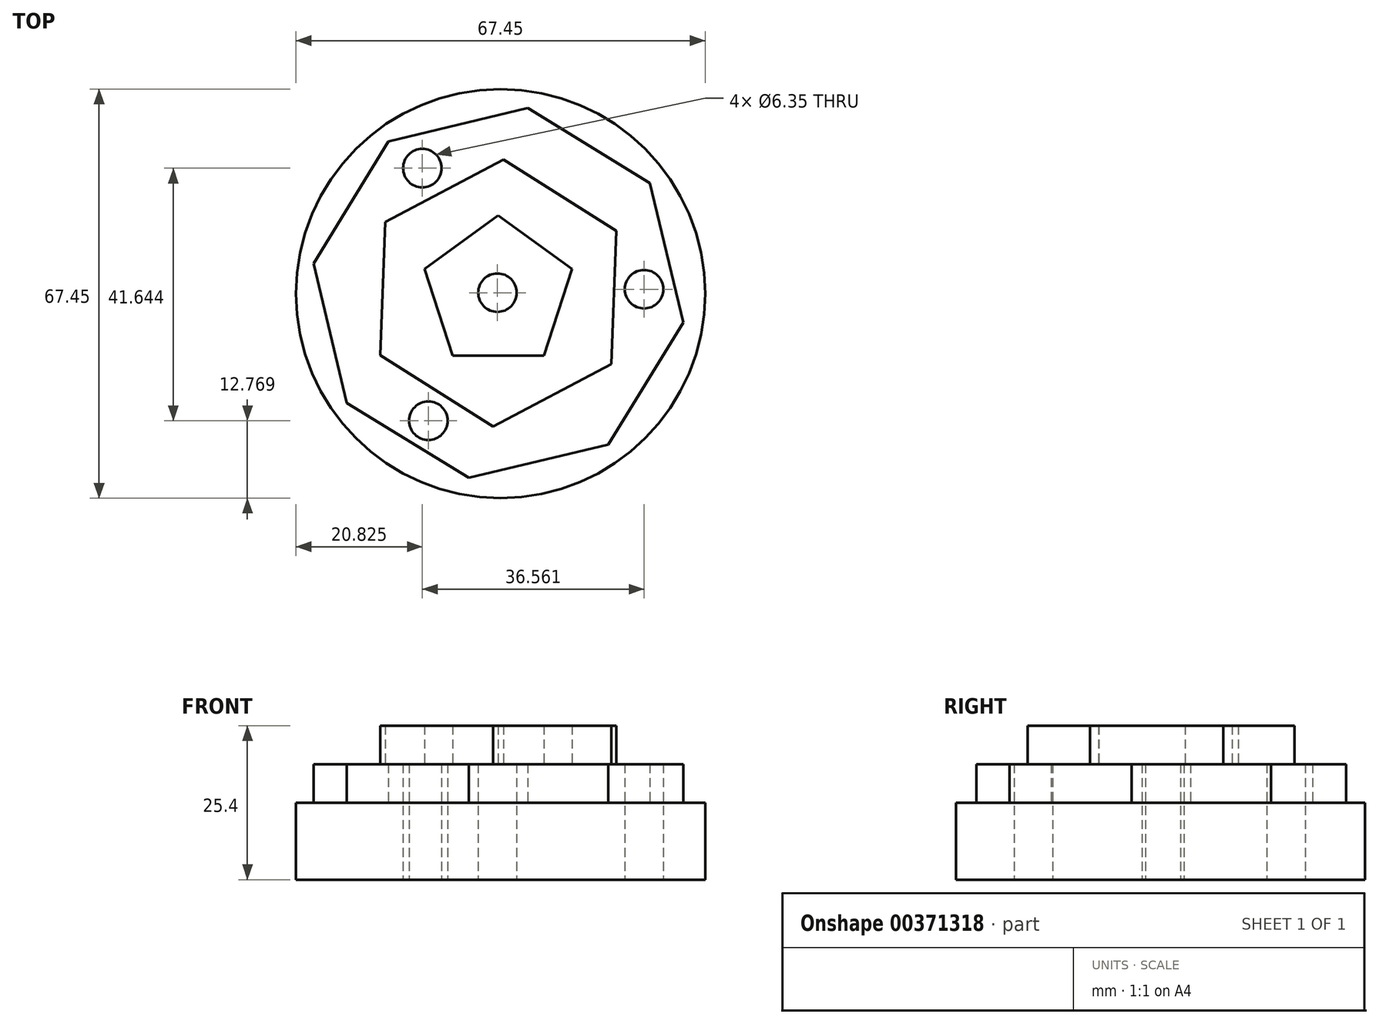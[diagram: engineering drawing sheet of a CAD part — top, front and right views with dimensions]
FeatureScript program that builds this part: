
annotation { "Feature Type Name" : "Feature", "Feature Type Description" : "" }
export const myFeature = defineFeature(function(context is Context, id is Id, definition is map)
    precondition{}
    {
        {
            var Q0;
            Q0=qCreatedBy(makeId("Top.planeOp"),FACE);
            var sketch = newSketch(context, id + "F0", { "sketchPlane" : qUnion([Q0])});
            skCircle(sketch, "E0", {"center": v(-39.3, -35.12) * mm, "radius": 33.73 * mm});
            skSolve(sketch);
        }
        {
            var Q0;
            Q0=makeQuery(id+"F0.imprint","IMPRINT",FACE,{"disambiguationData":[TD([[makeQuery(id+"F0.imprint","IMPRINT",EDGE,{"derivedFrom":sQuery(id+"F0.wireOp",EDGE,"E0")}),1.0]])]});
            var sketch = newSketch(context, id + "F1", { "sketchPlane" : qUnion([Q0])});
            skCircle(sketch, "E1.cCircle", {"center": v(-39.68, -35.03) * mm, "radius": 22.02 * mm, "construction": true});
            skLineSegment(sketch, "E1.0", {"start": v(-38.84, -13.02) * mm, "end": v(-21.05, -46.76) * mm});
            skLineSegment(sketch, "E1.1", {"start": v(-21.05, -46.76) * mm, "end": v(-59.16, -45.3) * mm});
            skLineSegment(sketch, "E1.2", {"start": v(-59.16, -45.3) * mm, "end": v(-38.84, -13.02) * mm});
            skCircle(sketch, "E2.cCircle", {"center": v(-39.68, -35.03) * mm, "radius": 12.76 * mm, "construction": true});
            skLineSegment(sketch, "E2.0", {"start": v(-39.68, -22.27) * mm, "end": v(-27.55, -31.08) * mm});
            skLineSegment(sketch, "E2.1", {"start": v(-27.55, -31.08) * mm, "end": v(-32.19, -45.35) * mm});
            skLineSegment(sketch, "E2.2", {"start": v(-32.19, -45.35) * mm, "end": v(-47.18, -45.35) * mm});
            skLineSegment(sketch, "E2.3", {"start": v(-47.18, -45.35) * mm, "end": v(-51.82, -31.08) * mm});
            skLineSegment(sketch, "E2.4", {"start": v(-51.82, -31.08) * mm, "end": v(-39.68, -22.27) * mm});
            skLineSegment(sketch, "E3.0", {"start": v(-38.84, -13.02) * mm, "end": v(-20.2, -24.76) * mm});
            skLineSegment(sketch, "E3.1", {"start": v(-20.2, -24.76) * mm, "end": v(-21.05, -46.76) * mm});
            skLineSegment(sketch, "E3.2", {"start": v(-21.05, -46.76) * mm, "end": v(-40.53, -57.03) * mm});
            skLineSegment(sketch, "E3.3", {"start": v(-40.53, -57.03) * mm, "end": v(-59.16, -45.3) * mm});
            skLineSegment(sketch, "E3.4", {"start": v(-59.16, -45.3) * mm, "end": v(-58.32, -23.3) * mm});
            skLineSegment(sketch, "E3.5", {"start": v(-58.32, -23.3) * mm, "end": v(-38.84, -13.02) * mm});
            skSolve(sketch);
        }
        {
            var Q0;
            Q0=qCreatedBy(makeId("Top.planeOp"),FACE);
            var sketch = newSketch(context, id + "F2", { "sketchPlane" : qUnion([Q0])});
            skCircle(sketch, "E4.cCircle", {"center": v(-39.67, -35.02) * mm, "radius": 28.5 * mm, "construction": true});
            skLineSegment(sketch, "E4.0", {"start": v(-34.83, -4.54) * mm, "end": v(-14.7, -16.9) * mm});
            skLineSegment(sketch, "E4.1", {"start": v(-14.7, -16.9) * mm, "end": v(-9.2, -39.86) * mm});
            skLineSegment(sketch, "E4.2", {"start": v(-9.2, -39.86) * mm, "end": v(-21.55, -60) * mm});
            skLineSegment(sketch, "E4.3", {"start": v(-21.55, -60) * mm, "end": v(-44.52, -65.5) * mm});
            skLineSegment(sketch, "E4.4", {"start": v(-44.52, -65.5) * mm, "end": v(-64.65, -53.14) * mm});
            skLineSegment(sketch, "E4.5", {"start": v(-64.65, -53.14) * mm, "end": v(-70.15, -30.17) * mm});
            skLineSegment(sketch, "E4.6", {"start": v(-70.15, -30.17) * mm, "end": v(-57.8, -10.04) * mm});
            skLineSegment(sketch, "E4.7", {"start": v(-57.8, -10.04) * mm, "end": v(-34.83, -4.54) * mm});
            skPoint(sketch, "E4.0.midPoint", {"position": v(-24.76, -10.72) * mm});
            skSolve(sketch);
        }
        {
            var Q0;
            Q0=makeQuery(id+"F0.imprint","IMPRINT",FACE,{"disambiguationData":[TD([[makeQuery(id+"F0.imprint","IMPRINT",EDGE,{"derivedFrom":sQuery(id+"F0.wireOp",EDGE,"E0")}),1.0]])]});
            var sketch = newSketch(context, id + "F3", { "sketchPlane" : qUnion([Q0])});
            skCircle(sketch, "E5.cCircle", {"center": v(-39.82, -34.97) * mm, "radius": 33.32 * mm, "construction": true});
            skLineSegment(sketch, "E5.0", {"start": v(-37.67, -1.72) * mm, "end": v(-16.8, -10.88) * mm});
            skLineSegment(sketch, "E5.1", {"start": v(-16.8, -10.88) * mm, "end": v(-6.7, -31.32) * mm});
            skLineSegment(sketch, "E5.2", {"start": v(-6.7, -31.32) * mm, "end": v(-12.1, -53.46) * mm});
            skLineSegment(sketch, "E5.3", {"start": v(-12.1, -53.46) * mm, "end": v(-30.47, -66.95) * mm});
            skLineSegment(sketch, "E5.4", {"start": v(-30.47, -66.95) * mm, "end": v(-53.22, -65.48) * mm});
            skLineSegment(sketch, "E5.5", {"start": v(-53.22, -65.48) * mm, "end": v(-69.7, -49.73) * mm});
            skLineSegment(sketch, "E5.6", {"start": v(-69.7, -49.73) * mm, "end": v(-72.2, -27.08) * mm});
            skLineSegment(sketch, "E5.7", {"start": v(-72.2, -27.08) * mm, "end": v(-59.55, -8.12) * mm});
            skLineSegment(sketch, "E5.8", {"start": v(-59.55, -8.12) * mm, "end": v(-37.67, -1.72) * mm});
            skSolve(sketch);
        }
        {
            var Q0;
            Q0=makeQuery(id+"F0.imprint","IMPRINT",FACE,{"disambiguationData":[TD([[makeQuery(id+"F0.imprint","IMPRINT",EDGE,{"derivedFrom":sQuery(id+"F0.wireOp",EDGE,"E0")}),1.0]])]});
            var sketch = newSketch(context, id + "F4", { "sketchPlane" : qUnion([Q0])});
            skCircle(sketch, "E6.cCircle", {"center": v(-39.69, -34.97) * mm, "radius": 24.05 * mm, "construction": true});
            skLineSegment(sketch, "E6.0", {"start": v(-52.2, -14.44) * mm, "end": v(-15.64, -34.4) * mm});
            skLineSegment(sketch, "E6.1", {"start": v(-15.64, -34.4) * mm, "end": v(-51.21, -56.08) * mm});
            skLineSegment(sketch, "E6.2", {"start": v(-51.21, -56.08) * mm, "end": v(-52.2, -14.44) * mm});
            skSolve(sketch);
        }
        {
            var Q0;
            Q0 = qSketchRegion(id + "F0", true);
            extrude(context, id + "F5", {"entities" : qUnion([Q0]), "depth" : 12.7 * mm});
        }
        {
            var Q0;
            Q0 = qSketchRegion(id + "F1", true);
            extrude(context, id + "F6", {"entities" : qUnion([Q0]), "operationType" : NewBodyOperationType.ADD, "depth" : 25.4 * mm});
        }
        {
            var Q0;
            Q0 = qSketchRegion(id + "F2", true);
            extrude(context, id + "F7", {"entities" : qUnion([Q0]), "operationType" : NewBodyOperationType.ADD, "depth" : 19.05 * mm});
        }
        {
            var Q0;
            Q0=sQuery(id+"F3.wireOp",VERTEX,"E5.cCircle.center");
            var Q1;
            Q1=sQuery(id+"F4.wireOp",VERTEX,"E6.2.end");
            var Q2;
            Q2=sQuery(id+"F4.wireOp",VERTEX,"E6.2.start");
            var Q3;
            Q3=sQuery(id+"F4.wireOp",VERTEX,"E6.1.start");
            var Q4;
            Q4=makeQuery(id+"F5.opExtrude","SWEPT_BODY",BODY,{"disambiguationData":[OSD([sQuery(id+"F0.wireOp",EDGE,"E0")])]});
            hole(context, id + "F8", {"style" : HoleStyle.SIMPLE, "endStyle" : HoleEndStyle.THROUGH, "oppositeDirection" : true, "holeDiameter" : 6.35 * mm, "isTappedThrough" : true, "tappedDepth" : 12.7 * mm, "tapClearance" : 3, "locations" : qUnion([Q0, Q1, Q2, Q3]), "scope" : qUnion([Q4])});
        }
    });
